# Revit family: Hand_Dryer-World_Dryer-SMARTdri
name_source: partatom
category: Specialty Equipment
revit_build: Autodesk Revit Architecture 2015 (Build: 20140606_1530(x64)
units: mm (PartAtom-declared; Revit-internal decimal feet)

## types (6) — shared parameters
Brochure = http://worlddryer.com
Clearance On = No
Depth = 0' - 3 13/16"
Height = 1' - 1"
Manufacturer = World Dryer
Motor Speed (RPM) = 23400
Number of Poles = 1
Power Factor = 1
Product Documentation Link = http://worlddryer.com
Product Name = SMARTdri
Product Page URL = http://worlddryer.com
Product data url = https://bimobject.com
URL = http://worlddryer.com
Void Height = 1' - 8"
Width = 0' - 9 5/16"

## per-type parameters (varying)
| type | Apparent Load | CFM | Cover Finish | Description | Frequency | Phase | Voltage | Voltage Note | Watts |
| Model K4 | 1250 VA | 100 CFM | Metal - World Dryer - Chrome Polished | High-Efficiency Intelligent Multi-Port Nozzle Hand Dryer | 60 Hz | 1 | 208 V | 208 / 240 V | 1250 W |
| Model K | 1200 VA | 100 CFM | Metal - World Dryer - Chrome Polished | High-Efficiency Intelligent Multi-Port Nozzle Hand Dryer | 60 Hz | 1 | 120 V | 110 / 120 V | 1200 W |
| Model K48 | 1200 VA | 100 CFM | Metal - World Dryer - Chrome Polished | High-Efficiency Intelligent Multi-Port Nozzle Hand Dryer | 50 Hz | 1 | 240 V | 220 / 240 V | 1200 W |
| Model K-Plus | 1200 VA | 78 CFM | Metal - World Dryer - Chrome Polished | High-Efficiency Intelligent Single-Port Nozzle Hand Dryer | 60 Hz | 1 | 120 V | 110 / 120 V | 1200 W |
| Model K4-Plus | 1250 VA | 78 CFM | Metal - World Dryer - Chrome Polished | High-Efficiency Intelligent Single-Port Nozzle Hand Dryer | 60 Hz | 1 | 208 V | 208 / 240 V | 1250 W |
| Model K48-Plus | 1200 VA | 78 CFM | Metal - World Dryer - Aluminum - White | High-Efficiency Intelligent Single-Port Nozzle Hand Dryer | 50 Hz | 2 | 240 V | 220 / 240 V | 1200 W |

note: column(s) folded — value = type name in every type: Model

## geometry (parser evidence)
native form markers: Blend x16, Sweep x4
no freeform markers — native parametric forms only
